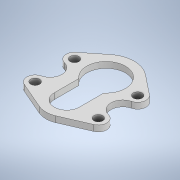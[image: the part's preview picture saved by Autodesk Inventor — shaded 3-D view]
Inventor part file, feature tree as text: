
AUTODESK INVENTOR PART (.ipt)
format: ipt  version: 2021 (Build 250183000, 183)  size: 154,112 bytes
history: native  units: mm
features: extrude x1, sketch x1
ambient origin geometry x8: Origin, YZ Plane, XZ Plane, XY Plane, X Axis, Y Axis, Z Axis, Center Point
bodies: Solid1 (feature_tree)
feature tree (2):
  extrude  "Extrusion1"  Depth=10.0mm
  sketch  "Sketch1"  dims[d0=94.0mm d1=70.0mm d2=66.0mm d3=0.0mm d4=28.0mm d5=28.0mm d6=53.0mm d7=0.0mm d8=0.0mm d9=66.0mm d10=40.0mm d11=42.0mm d12=65.0mm d13=15.0mm d14=15.0mm d15=10.0mm d16=0.0mm]
